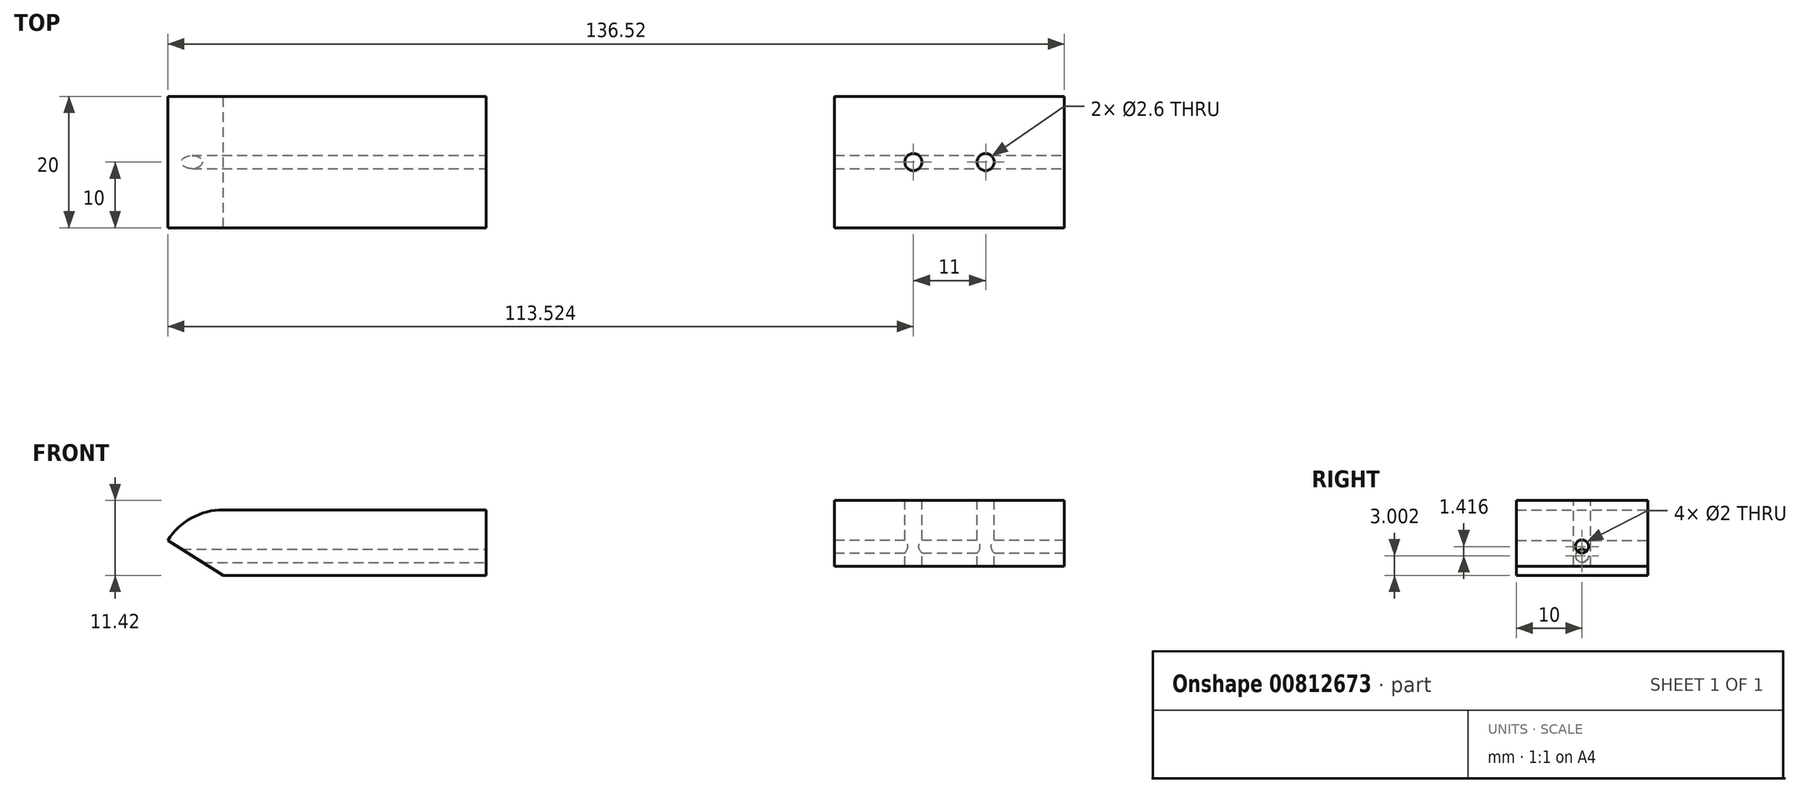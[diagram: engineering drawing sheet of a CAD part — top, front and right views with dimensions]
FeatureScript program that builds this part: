
annotation { "Feature Type Name" : "Feature", "Feature Type Description" : "" }
export const myFeature = defineFeature(function(context is Context, id is Id, definition is map)
    precondition{}
    {
        {
            var Q0;
            Q0=qCreatedBy(makeId("Front.planeOp"),FACE);
            var sketch = newSketch(context, id + "F0", { "sketchPlane" : qUnion([Q0])});
            skLineSegment(sketch, "E0", {"start": v(-78.33, 19.27) * mm, "end": v(-38.33, 19.27) * mm});
            skLineSegment(sketch, "E1", {"start": v(14.71, 20.69) * mm, "end": v(49.71, 20.69) * mm});
            skLineSegment(sketch, "E2.top", {"start": v(-78.33, 29.27) * mm, "end": v(-38.33, 29.27) * mm});
            skLineSegment(sketch, "E2.left", {"start": v(-78.33, 19.27) * mm, "end": v(-78.33, 29.27) * mm});
            skLineSegment(sketch, "E2.right", {"start": v(-38.33, 19.27) * mm, "end": v(-38.33, 29.27) * mm});
            skLineSegment(sketch, "E3.top", {"start": v(14.71, 30.69) * mm, "end": v(49.71, 30.69) * mm});
            skLineSegment(sketch, "E3.left", {"start": v(14.71, 20.69) * mm, "end": v(14.71, 30.69) * mm});
            skLineSegment(sketch, "E3.right", {"start": v(49.71, 20.69) * mm, "end": v(49.71, 30.69) * mm});
            skLineSegment(sketch, "E4", {"start": v(-78.33, 19.27) * mm, "end": v(-86.8, 24.59) * mm});
            skArc(sketch, "E5", {"start": v(-78.33, 29.27) * mm, "mid": v(-83.17, 28.02) * mm, "end": v(-86.8, 24.59) * mm});
            skSolve(sketch);
        }
        {
            var Q0;
            Q0 = qSketchRegion(id + "F0", true);
            extrude(context, id + "F1", {"entities" : qUnion([Q0]), "depth" : 20 * mm, "offsetDistance" : 25.4 * mm});
        }
        {
            var Q0;
            Q0=makeQuery(id+"F1.opExtrude","SWEPT_FACE",FACE,{"disambiguationData":[OSD([sQuery(id+"F0.wireOp",EDGE,"E2.right")])]});
            var sketch = newSketch(context, id + "F2", { "sketchPlane" : qUnion([Q0])});
            skCircle(sketch, "E6", {"center": v(-10, 22.27) * mm, "radius": 1 * mm});
            skSolve(sketch);
        }
        {
            var Q0;
            Q0 = qSketchRegion(id + "F2", true);
            extrude(context, id + "F3", {"entities" : qUnion([Q0]), "operationType" : NewBodyOperationType.REMOVE, "oppositeDirection" : true, "depth" : 58.17 * mm, "offsetDistance" : 25.4 * mm});
        }
        {
            var Q0;
            Q0=makeQuery(id+"F1.opExtrude","SWEPT_FACE",FACE,{"disambiguationData":[OSD([sQuery(id+"F0.wireOp",EDGE,"E3.right")])]});
            var sketch = newSketch(context, id + "F4", { "sketchPlane" : qUnion([Q0])});
            skCircle(sketch, "E7", {"center": v(-10, 23.69) * mm, "radius": 1 * mm});
            skSolve(sketch);
        }
        {
            var Q0;
            Q0 = qSketchRegion(id + "F4", true);
            extrude(context, id + "F5", {"entities" : qUnion([Q0]), "operationType" : NewBodyOperationType.REMOVE, "oppositeDirection" : true, "depth" : 44.98 * mm, "offsetDistance" : 25.4 * mm});
        }
        {
            var Q0;
            Q0=makeQuery(id+"F1.opExtrude","SWEPT_FACE",FACE,{"disambiguationData":[OSD([sQuery(id+"F0.wireOp",EDGE,"E3.top")])]});
            var sketch = newSketch(context, id + "F6", { "sketchPlane" : qUnion([Q0])});
            skPoint(sketch, "E8.endSnap0", {"position": v(49.71, -10) * mm});
            skCircle(sketch, "E9", {"center": v(26.71, -10) * mm, "radius": 1.3 * mm});
            skCircle(sketch, "E10", {"center": v(37.71, -10) * mm, "radius": 1.3 * mm});
            skSolve(sketch);
        }
        {
            var Q0;
            Q0 = qSketchRegion(id + "F6", true);
            extrude(context, id + "F7", {"entities" : qUnion([Q0]), "operationType" : NewBodyOperationType.REMOVE, "oppositeDirection" : true, "depth" : 25.4 * mm, "offsetDistance" : 25.4 * mm});
        }
    });
